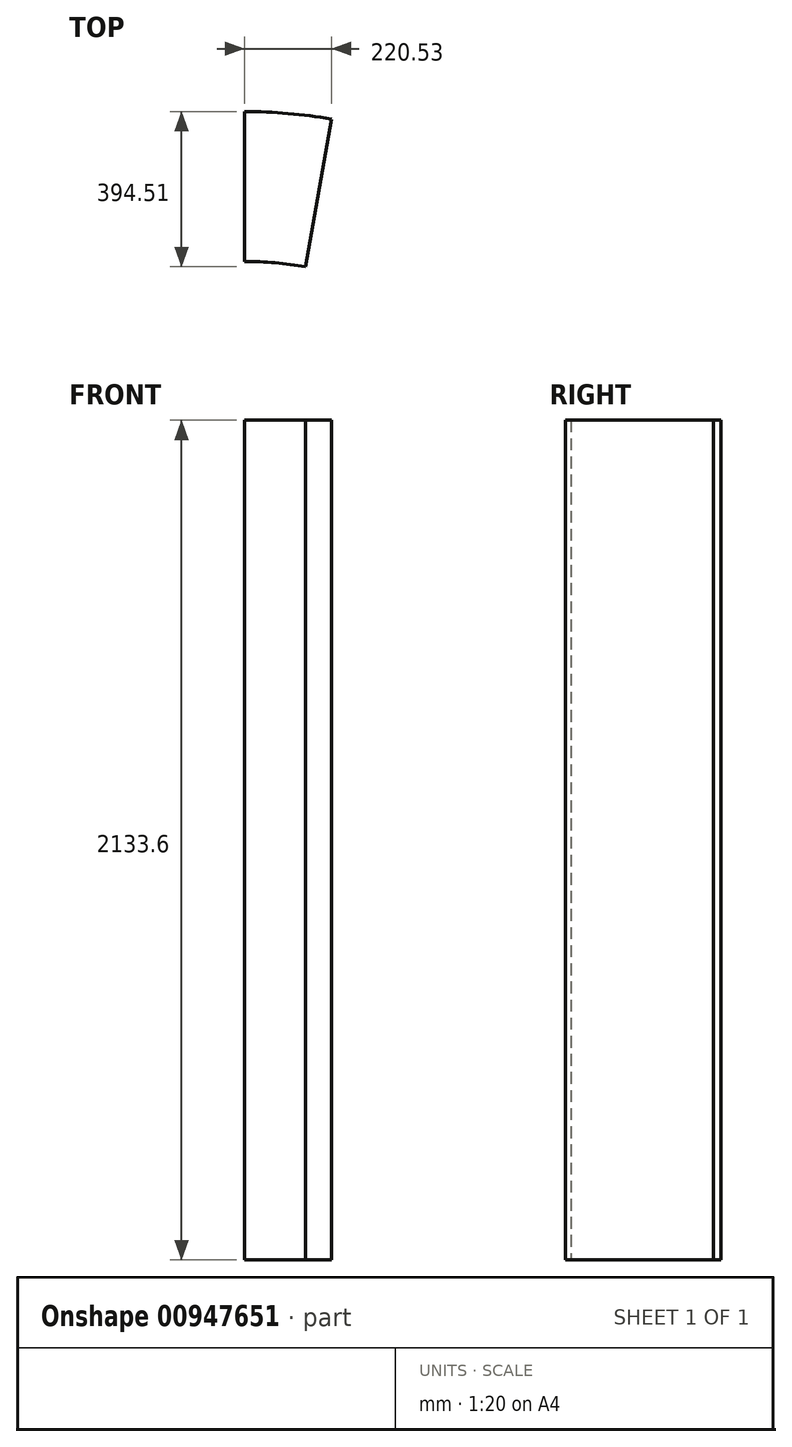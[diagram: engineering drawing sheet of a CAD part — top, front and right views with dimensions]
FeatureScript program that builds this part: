
annotation { "Feature Type Name" : "Feature", "Feature Type Description" : "" }
export const myFeature = defineFeature(function(context is Context, id is Id, definition is map)
    precondition{}
    {
        {
            var Q0;
            Q0=qCreatedBy(makeId("Top.planeOp"),FACE);
            var sketch = newSketch(context, id + "F0", { "sketchPlane" : qUnion([Q0])});
            skCircle(sketch, "E0", {"center": v(0, 0) * mm, "radius": 1270 * mm});
            skCircle(sketch, "E1", {"center": v(0, 0) * mm, "radius": 889 * mm});
            skSolve(sketch);
        }
        {
            var Q0;
            Q0=qCreatedBy(makeId("Top.planeOp"),FACE);
            var sketch = newSketch(context, id + "F1", { "sketchPlane" : qUnion([Q0])});
            skArc(sketch, "E2.0", {"start": v(220.53, 1250.7) * mm, "mid": v(110.69, 1265.17) * mm, "end": v(0, 1270) * mm});
            skArc(sketch, "E3.0", {"start": v(154.37, 875.5) * mm, "mid": v(77.48, 885.62) * mm, "end": v(0, 889) * mm});
            skLineSegment(sketch, "E4", {"start": v(0, 1270) * mm, "end": v(0, 889) * mm});
            skLineSegment(sketch, "E5", {"start": v(154.37, 875.5) * mm, "end": v(220.53, 1250.7) * mm});
            skSolve(sketch);
        }
        {
            var Q0;
            Q0=makeQuery(id+"F1.imprint","IMPRINT",FACE,{"disambiguationData":[TD([[makeQuery(id+"F1.imprint","IMPRINT",EDGE,{"derivedFrom":sQuery(id+"F1.wireOp",EDGE,"E2.0")}),1.0]])]});
            extrude(context, id + "F2", {"entities" : qUnion([Q0]), "depth" : 2133.6 * mm, "offsetDistance" : 25.4 * mm});
        }
    });
